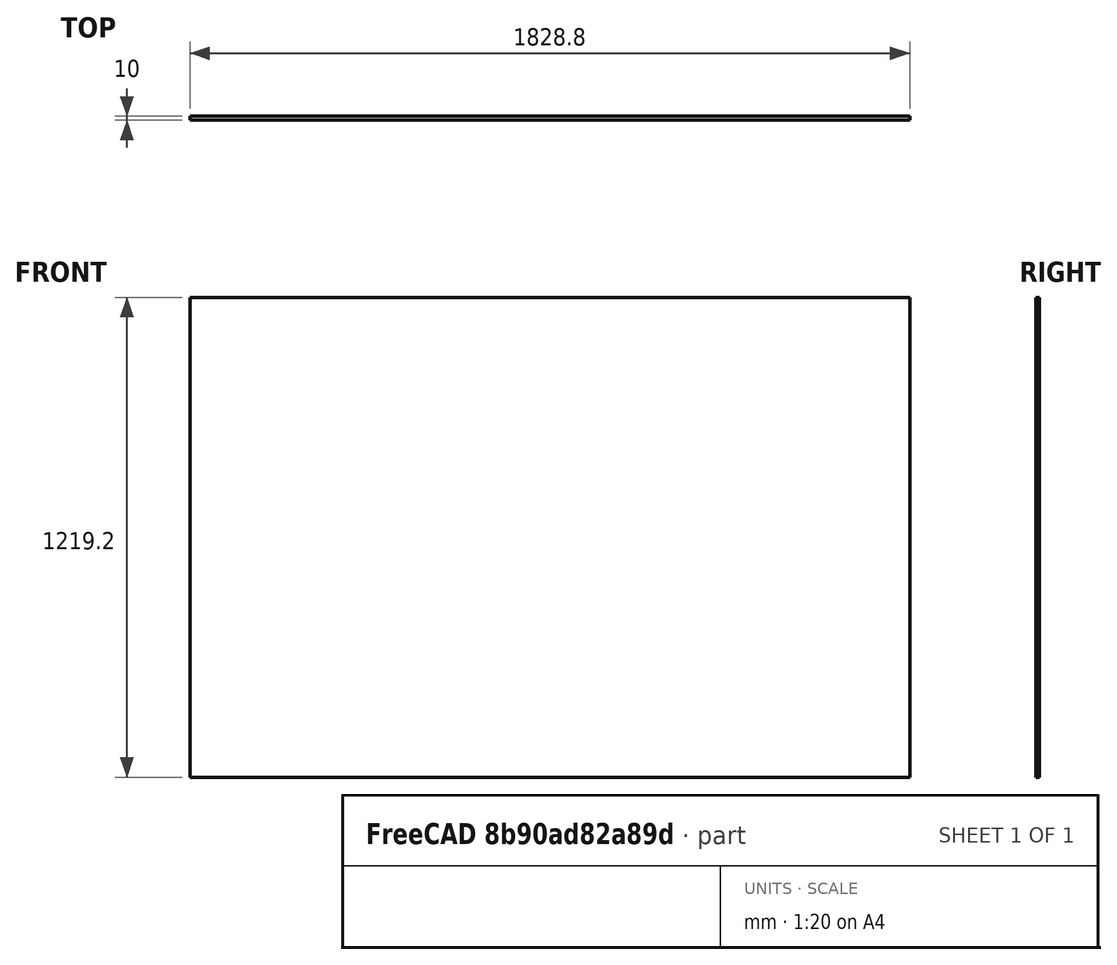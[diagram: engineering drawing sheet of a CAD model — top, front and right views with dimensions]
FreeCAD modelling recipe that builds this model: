
FCSTD DOCUMENT  (FreeCAD 0.19R24291 (Git))
Label: whiteBoard-6x4
License: All rights reserved
LicenseURL: http://en.wikipedia.org/wiki/All_rights_reserved
objects: Sketcher::SketchObject×1, PartDesign::Pad×1, PartDesign::Body×1
note: 4 computed .brp shape members not serialized (recipe doc carries the construction recipe); baked Part::Feature solids carry a one-line shape summary decoded from their .brp

FEATURE [Sketcher::SketchObject] Sketch
  FullyConstrained = true
  MapMode = 5
  Placement = pos=(0,0,0) rot=(1,0,0;1.5708rad)
  Support = -> [XZ_Plane]
  expr: Constraints[10] = 48 * 25.4
  expr: Constraints[9] = 6 * 12 * 25.4
  sketch-geometry (4):
    g0: LineSegment StartX=0 StartY=0 StartZ=0 EndX=1828.8 EndY=0 EndZ=0
    g1: LineSegment StartX=1828.8 StartY=0 StartZ=0 EndX=1828.8 EndY=1219.2 EndZ=0
    g2: LineSegment StartX=1828.8 StartY=1219.2 StartZ=0 EndX=0 EndY=1219.2 EndZ=0
    g3: LineSegment StartX=0 StartY=1219.2 StartZ=0 EndX=0 EndY=0 EndZ=0
  constraints (11):
    c: Coincident(g0,g1)
    c: Coincident(g1,g2)
    c: Coincident(g2,g3)
    c: Coincident(g3,g0)
    c: Horizontal(g0)
    c: Horizontal(g2)
    c: Vertical(g1)
    c: Vertical(g3)
    c: Coincident(g0,g-1)
    c: DistanceX(g0,g0) = 1828.8
    c: DistanceY(g3,g3) = 1219.2
FEATURE [PartDesign::Pad] Pad
  Direction = (1,1,1)
  Length = 10
  Length2 = 100
  Placement = pos=(0,0,0) rot=(1,0,0;1.5708rad)
  Profile = -> Sketch
  Type = 0
FEATURE [PartDesign::Body] Body
  Group = -> [Sketch,Pad]
  Origin = -> Origin
  Tip = -> Pad
